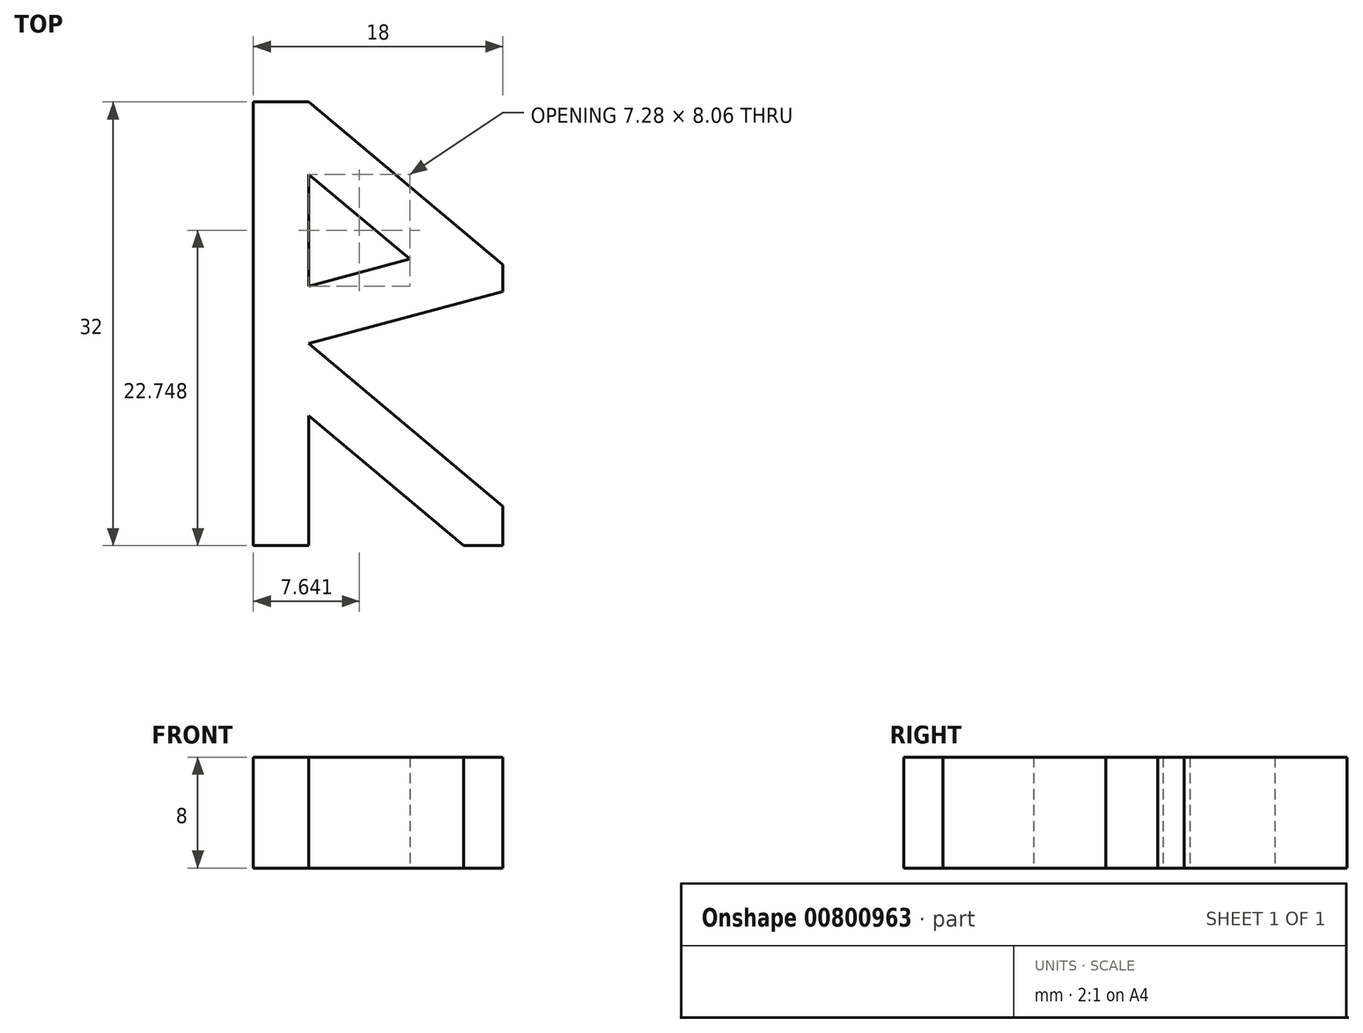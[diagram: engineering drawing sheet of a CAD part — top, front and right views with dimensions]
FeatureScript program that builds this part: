
annotation { "Feature Type Name" : "Feature", "Feature Type Description" : "" }
export const myFeature = defineFeature(function(context is Context, id is Id, definition is map)
    precondition{}
    {
        {
            var Q0;
            Q0=qCreatedBy(makeId("Top.planeOp"),FACE);
            var sketch = newSketch(context, id + "F0", { "sketchPlane" : qUnion([Q0])});
            skLineSegment(sketch, "E0", {"start": v(0, 0) * mm, "end": v(0, -32) * mm});
            skLineSegment(sketch, "E1", {"start": v(0, -32) * mm, "end": v(4, -32) * mm});
            skLineSegment(sketch, "E2", {"start": v(4, -32) * mm, "end": v(4, -22.63) * mm});
            skLineSegment(sketch, "E3", {"start": v(4, -22.63) * mm, "end": v(15.17, -32) * mm});
            skLineSegment(sketch, "E4", {"start": v(15.17, -32) * mm, "end": v(18, -32) * mm});
            skLineSegment(sketch, "E5", {"start": v(18, -32) * mm, "end": v(18, -29.17) * mm});
            skLineSegment(sketch, "E6", {"start": v(18, -29.17) * mm, "end": v(4, -17.42) * mm});
            skLineSegment(sketch, "E7", {"start": v(4, 0) * mm, "end": v(0, 0) * mm});
            skLineSegment(sketch, "E8", {"start": v(4, -5.22) * mm, "end": v(4, -13.28) * mm});
            skLineSegment(sketch, "E9", {"start": v(4, -13.28) * mm, "end": v(11.28, -11.33) * mm});
            skLineSegment(sketch, "E10", {"start": v(11.28, -11.33) * mm, "end": v(4, -5.22) * mm});
            skLineSegment(sketch, "E11", {"start": v(4, 0) * mm, "end": v(18, -11.75) * mm});
            skLineSegment(sketch, "E12", {"start": v(18, -11.75) * mm, "end": v(18, -13.67) * mm});
            skLineSegment(sketch, "E13", {"start": v(18, -13.67) * mm, "end": v(4, -17.42) * mm});
            skLineSegment(sketch, "E14", {"start": v(18, -29.17) * mm, "end": v(18, -13.67) * mm, "construction": true});
            skSolve(sketch);
        }
        {
            var Q0;
            Q0 = qSketchRegion(id + "F0", true);
            extrude(context, id + "F1", {"entities" : qUnion([Q0]), "depth" : 8 * mm, "offsetDistance" : 25 * mm});
        }
    });
